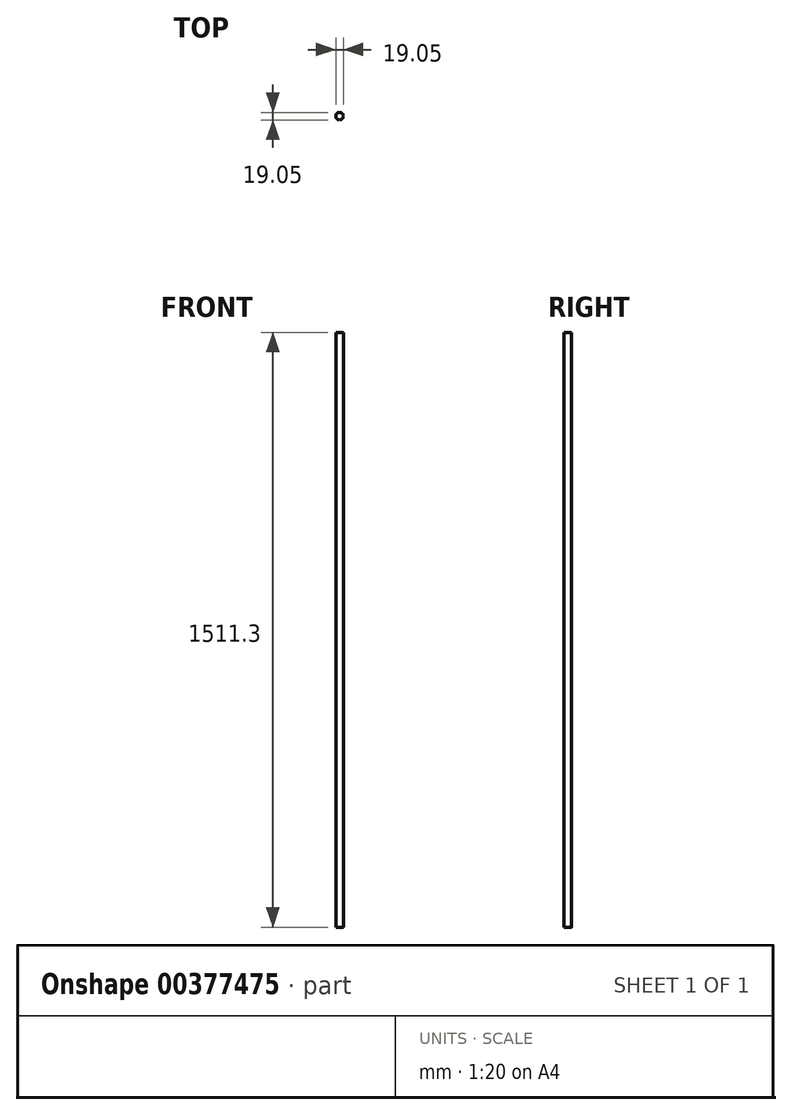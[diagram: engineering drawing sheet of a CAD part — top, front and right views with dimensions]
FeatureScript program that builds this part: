
annotation { "Feature Type Name" : "Feature", "Feature Type Description" : "" }
export const myFeature = defineFeature(function(context is Context, id is Id, definition is map)
    precondition{}
    {
        {
            var Q0;
            Q0=qCreatedBy(makeId("Top.planeOp"),FACE);
            var sketch = newSketch(context, id + "F0", { "sketchPlane" : qUnion([Q0])});
            skCircle(sketch, "E0", {"center": v(-123.6, -11.81) * mm, "radius": 9.53 * mm});
            skSolve(sketch);
        }
        {
            var Q0;
            Q0=makeQuery(id+"F0.imprint","IMPRINT",FACE,{"disambiguationData":[TD([[makeQuery(id+"F0.imprint","IMPRINT",EDGE,{"derivedFrom":sQuery(id+"F0.wireOp",EDGE,"E0")}),1.0]])]});
            extrude(context, id + "F1", {"entities" : qUnion([Q0]), "depth" : 1511.3 * mm});
        }
    });
